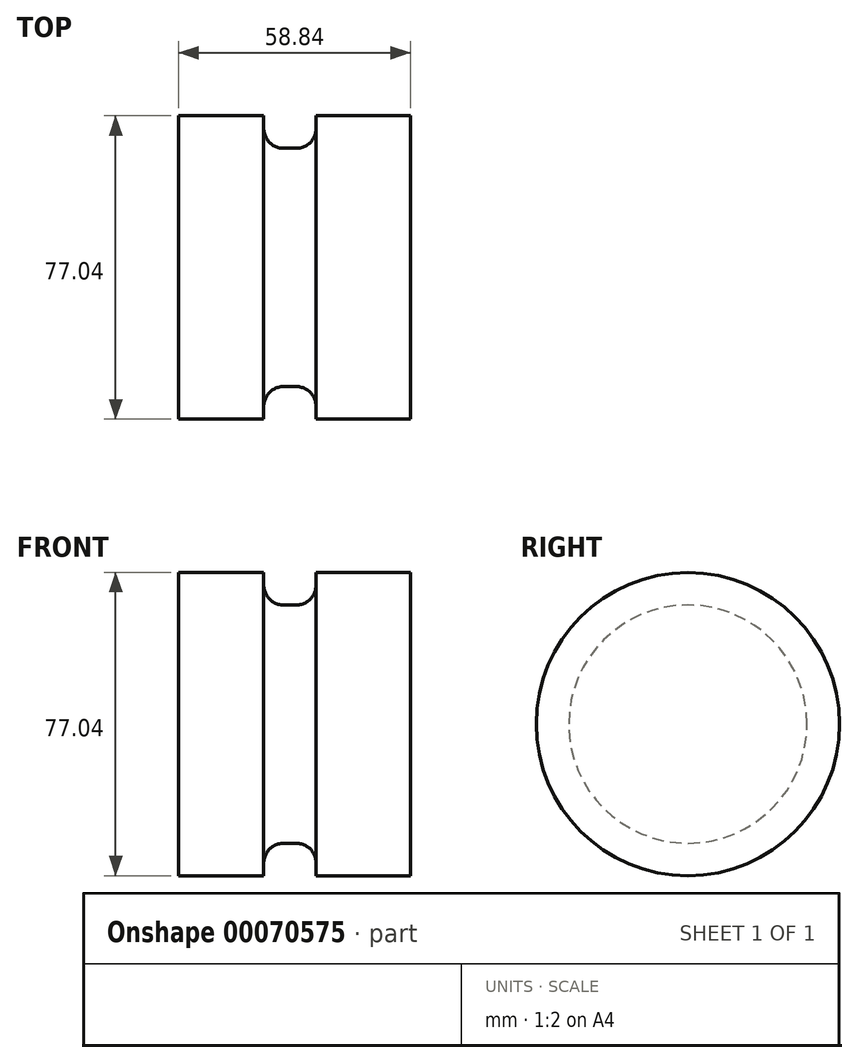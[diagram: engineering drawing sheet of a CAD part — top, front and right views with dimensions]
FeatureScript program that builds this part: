
annotation { "Feature Type Name" : "Feature", "Feature Type Description" : "" }
export const myFeature = defineFeature(function(context is Context, id is Id, definition is map)
    precondition{}
    {
        {
            var Q0;
            Q0=qCreatedBy(makeId("Front.planeOp"),FACE);
            var sketch = newSketch(context, id + "F0", { "sketchPlane" : qUnion([Q0])});
            skLineSegment(sketch, "E0.bottom", {"start": v(0, 0) * mm, "end": v(58.84, 0) * mm});
            skLineSegment(sketch, "E0.top", {"start": v(0, 38.52) * mm, "end": v(58.84, 38.52) * mm});
            skLineSegment(sketch, "E0.left", {"start": v(0, 0) * mm, "end": v(0, 38.52) * mm});
            skLineSegment(sketch, "E0.right", {"start": v(58.84, 0) * mm, "end": v(58.84, 38.52) * mm});
            skSolve(sketch);
        }
        {
            var Q0;
            Q0 = qSketchRegion(id + "F0", true);
            var Q1;
            Q1=sQuery(id+"F0.wireOp",EDGE,"E0.bottom");
            revolve(context, id + "F1", {"entities" : qUnion([Q0]), "axis" : qUnion([Q1]), "revolveType" : RevolveType.FULL});
        }
        {
            var Q0;
            Q0=qCreatedBy(makeId("Front.planeOp"),FACE);
            var sketch = newSketch(context, id + "F2", { "sketchPlane" : qUnion([Q0])});
            skLineSegment(sketch, "E1.bottom", {"start": v(21.6, 30.27) * mm, "end": v(34.93, 30.27) * mm});
            skLineSegment(sketch, "E1.top", {"start": v(21.6, 41.49) * mm, "end": v(34.93, 41.49) * mm});
            skLineSegment(sketch, "E1.left", {"start": v(21.6, 30.27) * mm, "end": v(21.6, 41.49) * mm});
            skLineSegment(sketch, "E1.right", {"start": v(34.93, 30.27) * mm, "end": v(34.93, 41.49) * mm});
            skLineSegment(sketch, "E2", {"start": v(0, 0) * mm, "end": v(64.56, 0) * mm});
            skSolve(sketch);
        }
        {
            var Q0;
            Q0 = qSketchRegion(id + "F2", true);
            var Q1;
            Q1=sQuery(id+"F2.wireOp",EDGE,"E2");
            revolve(context, id + "F3", {"operationType" : NewBodyOperationType.REMOVE, "entities" : qUnion([Q0]), "axis" : qUnion([Q1]), "revolveType" : RevolveType.FULL, "oppositeDirection" : true});
        }
        {
            var Q0;
            Q0=makeQuery(id+"F3.boolean.opBoolean","COPY",FACE,{"derivedFrom":makeQuery(id+"F3.opRevolve","SWEPT_FACE",FACE,{"disambiguationData":[OSD([sQuery(id+"F2.wireOp",EDGE,"E1.bottom")])]})});
            fillet(context, id + "F4", {"entities" : qUnion([Q0]), "radius" : 5.08 * mm, "tangentPropagation" : true, "allowEdgeOverflow" : false});
        }
    });
